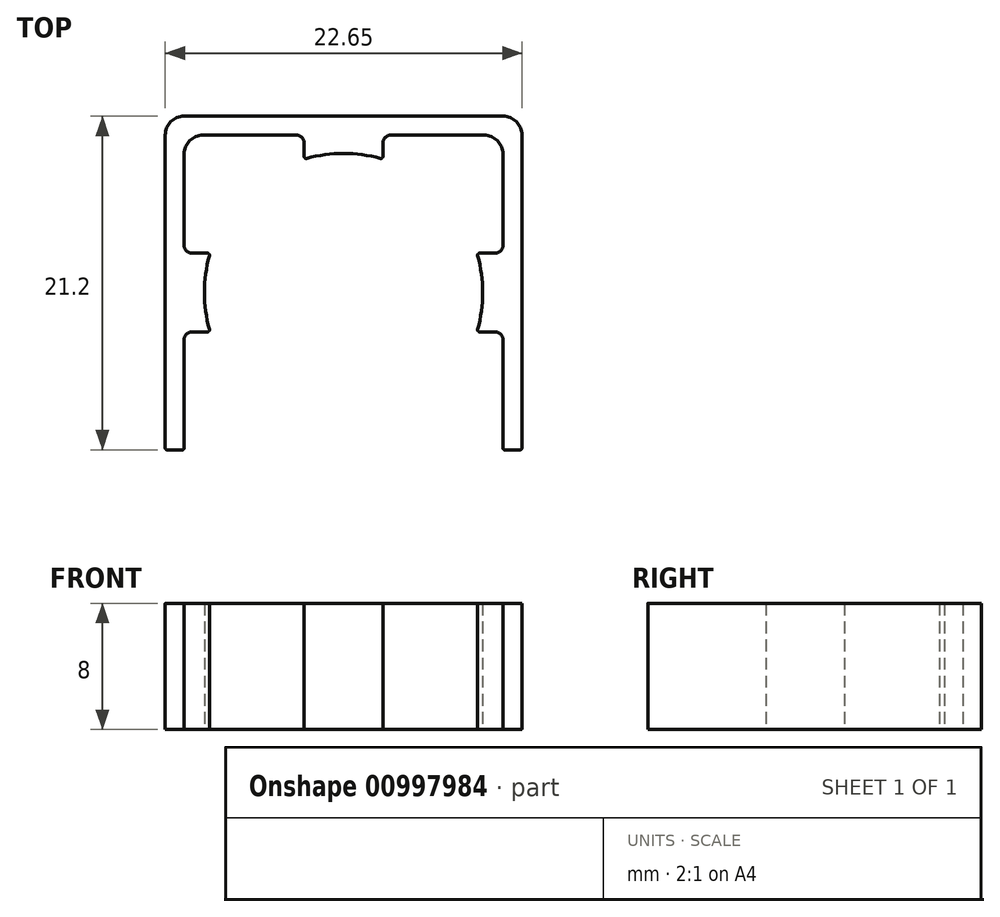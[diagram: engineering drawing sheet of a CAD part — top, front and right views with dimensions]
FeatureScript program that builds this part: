
annotation { "Feature Type Name" : "Feature", "Feature Type Description" : "" }
export const myFeature = defineFeature(function(context is Context, id is Id, definition is map)
    precondition{}
    {
        {
            var Q0;
            Q0=qCreatedBy(makeId("Top.planeOp"),FACE);
            var sketch = newSketch(context, id + "F0", { "sketchPlane" : qUnion([Q0])});
            skLineSegment(sketch, "E0", {"start": v(-3.94, -8.29) * mm, "end": v(-3.94, 11.59) * mm});
            skLineSegment(sketch, "E1", {"start": v(-2.74, 12.79) * mm, "end": v(17.5, 12.79) * mm});
            skLineSegment(sketch, "E2", {"start": v(18.7, 11.59) * mm, "end": v(18.7, -8.29) * mm});
            skLineSegment(sketch, "E3", {"start": v(18.58, -8.41) * mm, "end": v(17.63, -8.41) * mm});
            skLineSegment(sketch, "E4", {"start": v(17.5, -8.29) * mm, "end": v(17.5, -1.41) * mm});
            skLineSegment(sketch, "E5", {"start": v(16.3, 11.59) * mm, "end": v(10.38, 11.59) * mm});
            skLineSegment(sketch, "E6", {"start": v(-2.74, 10.39) * mm, "end": v(-2.74, 4.59) * mm});
            skLineSegment(sketch, "E7", {"start": v(-2.87, -8.41) * mm, "end": v(-3.82, -8.41) * mm});
            skPoint(sketch, "E8", {"position": v(4.88, 11.59) * mm});
            skPoint(sketch, "E9", {"position": v(9.88, 11.59) * mm});
            skPoint(sketch, "E10", {"position": v(-2.74, 4.09) * mm});
            skPoint(sketch, "E11", {"position": v(-2.74, -0.91) * mm});
            skPoint(sketch, "E12", {"position": v(17.5, 4.09) * mm});
            skPoint(sketch, "E13", {"position": v(17.5, -0.91) * mm});
            skLineSegment(sketch, "E14.bottom", {"start": v(-2.24, 4.09) * mm, "end": v(-1.26, 4.09) * mm});
            skLineSegment(sketch, "E14.top", {"start": v(-2.24, -0.91) * mm, "end": v(-1.26, -0.91) * mm});
            skLineSegment(sketch, "E15.bottom", {"start": v(17, 4.09) * mm, "end": v(16.02, 4.09) * mm});
            skLineSegment(sketch, "E15.top", {"start": v(17, -0.91) * mm, "end": v(16.02, -0.91) * mm});
            skLineSegment(sketch, "E16.left", {"start": v(4.88, 11.09) * mm, "end": v(4.88, 10.23) * mm});
            skLineSegment(sketch, "E16.right", {"start": v(9.88, 11.09) * mm, "end": v(9.88, 10.23) * mm});
            skLineSegment(sketch, "E17", {"start": v(-0.74, 1.59) * mm, "end": v(15.5, 1.59) * mm, "construction": true});
            skPoint(sketch, "E18", {"position": v(-1.1, -0.91) * mm});
            skPoint(sketch, "E19", {"position": v(7.38, 1.59) * mm});
            skArc(sketch, "E20", {"start": v(-1.14, 3.93) * mm, "mid": v(-1.45, 1.59) * mm, "end": v(-1.14, -0.76) * mm});
            skPoint(sketch, "E21.orphan", {"position": v(-0.74, 4.09) * mm});
            skPoint(sketch, "E14.right.end.orphan", {"position": v(-0.74, -0.91) * mm});
            skArc(sketch, "E22.trimOffspring", {"start": v(15.9, -0.76) * mm, "mid": v(16.22, 1.59) * mm, "end": v(15.9, 3.93) * mm});
            skPoint(sketch, "E23.orphan", {"position": v(9.88, 9.59) * mm});
            skArc(sketch, "E24.trimOffspring", {"start": v(9.72, 10.1) * mm, "mid": v(7.38, 10.42) * mm, "end": v(5.04, 10.1) * mm});
            skPoint(sketch, "E25.orphan", {"position": v(15.5, 4.09) * mm});
            skPoint(sketch, "E26.orphan", {"position": v(15.5, -0.91) * mm});
            skLineSegment(sketch, "E27.trimOffspring", {"start": v(17.5, 4.59) * mm, "end": v(17.5, 10.39) * mm});
            skLineSegment(sketch, "E28.trimOffspring", {"start": v(4.38, 11.59) * mm, "end": v(-1.54, 11.59) * mm});
            skLineSegment(sketch, "E29.trimOffspring", {"start": v(-2.74, -1.41) * mm, "end": v(-2.74, -8.29) * mm});
            skPoint(sketch, "E30.visualSharp", {"position": v(-2.74, 11.59) * mm});
            skArc(sketch, "E30.filletArc", {"start": v(-1.54, 11.59) * mm, "mid": v(-2.4, 11.23) * mm, "end": v(-2.74, 10.39) * mm});
            skPoint(sketch, "E31.visualSharp", {"position": v(17.5, 11.59) * mm});
            skArc(sketch, "E31.filletArc", {"start": v(17.5, 10.39) * mm, "mid": v(17.15, 11.23) * mm, "end": v(16.3, 11.59) * mm});
            skPoint(sketch, "E32.visualSharp", {"position": v(-3.94, 12.79) * mm});
            skArc(sketch, "E32.filletArc", {"start": v(-2.74, 12.79) * mm, "mid": v(-3.6, 12.43) * mm, "end": v(-3.94, 11.59) * mm});
            skPoint(sketch, "E33.visualSharp", {"position": v(18.7, 12.79) * mm});
            skArc(sketch, "E33.filletArc", {"start": v(18.7, 11.59) * mm, "mid": v(18.35, 12.43) * mm, "end": v(17.5, 12.79) * mm});
            skArc(sketch, "E34.filletArc", {"start": v(-2.74, 4.59) * mm, "mid": v(-2.6, 4.23) * mm, "end": v(-2.24, 4.09) * mm});
            skArc(sketch, "E35.filletArc", {"start": v(-2.24, -0.91) * mm, "mid": v(-2.6, -1.06) * mm, "end": v(-2.74, -1.41) * mm});
            skArc(sketch, "E36.filletArc", {"start": v(4.88, 11.09) * mm, "mid": v(4.73, 11.44) * mm, "end": v(4.38, 11.59) * mm});
            skArc(sketch, "E37.filletArc", {"start": v(10.38, 11.59) * mm, "mid": v(10.03, 11.44) * mm, "end": v(9.88, 11.09) * mm});
            skArc(sketch, "E38.filletArc", {"start": v(17, 4.09) * mm, "mid": v(17.36, 4.23) * mm, "end": v(17.5, 4.59) * mm});
            skArc(sketch, "E39.filletArc", {"start": v(17.5, -1.41) * mm, "mid": v(17.36, -1.06) * mm, "end": v(17, -0.91) * mm});
            skPoint(sketch, "E40.visualSharp", {"position": v(15.86, 4.09) * mm});
            skArc(sketch, "E40.filletArc", {"start": v(16.02, 4.09) * mm, "mid": v(15.92, 4.04) * mm, "end": v(15.9, 3.93) * mm});
            skPoint(sketch, "E41.visualSharp", {"position": v(15.86, -0.91) * mm});
            skArc(sketch, "E41.filletArc", {"start": v(15.9, -0.76) * mm, "mid": v(15.92, -0.86) * mm, "end": v(16.02, -0.91) * mm});
            skArc(sketch, "E42.filletArc", {"start": v(-1.26, -0.91) * mm, "mid": v(-1.16, -0.86) * mm, "end": v(-1.14, -0.76) * mm});
            skPoint(sketch, "E43.visualSharp", {"position": v(-1.1, 4.09) * mm});
            skArc(sketch, "E43.filletArc", {"start": v(-1.14, 3.93) * mm, "mid": v(-1.16, 4.04) * mm, "end": v(-1.26, 4.09) * mm});
            skPoint(sketch, "E44.visualSharp", {"position": v(4.88, 10.06) * mm});
            skArc(sketch, "E44.filletArc", {"start": v(4.88, 10.23) * mm, "mid": v(4.93, 10.13) * mm, "end": v(5.04, 10.1) * mm});
            skPoint(sketch, "E45.visualSharp", {"position": v(9.88, 10.06) * mm});
            skArc(sketch, "E45.filletArc", {"start": v(9.72, 10.1) * mm, "mid": v(9.83, 10.13) * mm, "end": v(9.88, 10.23) * mm});
            skPoint(sketch, "E46.visualSharp", {"position": v(-3.94, -8.41) * mm});
            skArc(sketch, "E46.filletArc", {"start": v(-3.94, -8.29) * mm, "mid": v(-3.9, -8.38) * mm, "end": v(-3.82, -8.41) * mm});
            skPoint(sketch, "E47.visualSharp", {"position": v(-2.74, -8.41) * mm});
            skArc(sketch, "E47.filletArc", {"start": v(-2.87, -8.41) * mm, "mid": v(-2.78, -8.38) * mm, "end": v(-2.74, -8.29) * mm});
            skPoint(sketch, "E48.visualSharp", {"position": v(17.5, -8.41) * mm});
            skArc(sketch, "E48.filletArc", {"start": v(17.5, -8.29) * mm, "mid": v(17.54, -8.38) * mm, "end": v(17.63, -8.41) * mm});
            skPoint(sketch, "E49.visualSharp", {"position": v(18.7, -8.41) * mm});
            skArc(sketch, "E49.filletArc", {"start": v(18.58, -8.41) * mm, "mid": v(18.67, -8.38) * mm, "end": v(18.7, -8.29) * mm});
            skSolve(sketch);
        }
        {
            var Q0;
            Q0=makeQuery(id+"F0.imprint","IMPRINT",FACE,{"disambiguationData":[TD([[makeQuery(id+"F0.imprint","IMPRINT",EDGE,{"derivedFrom":sQuery(id+"F0.wireOp",EDGE,"E0")}),-1.0]])]});
            extrude(context, id + "F1", {"entities" : qUnion([Q0]), "depth" : 8 * mm, "offsetDistance" : 25 * mm});
        }
    });
